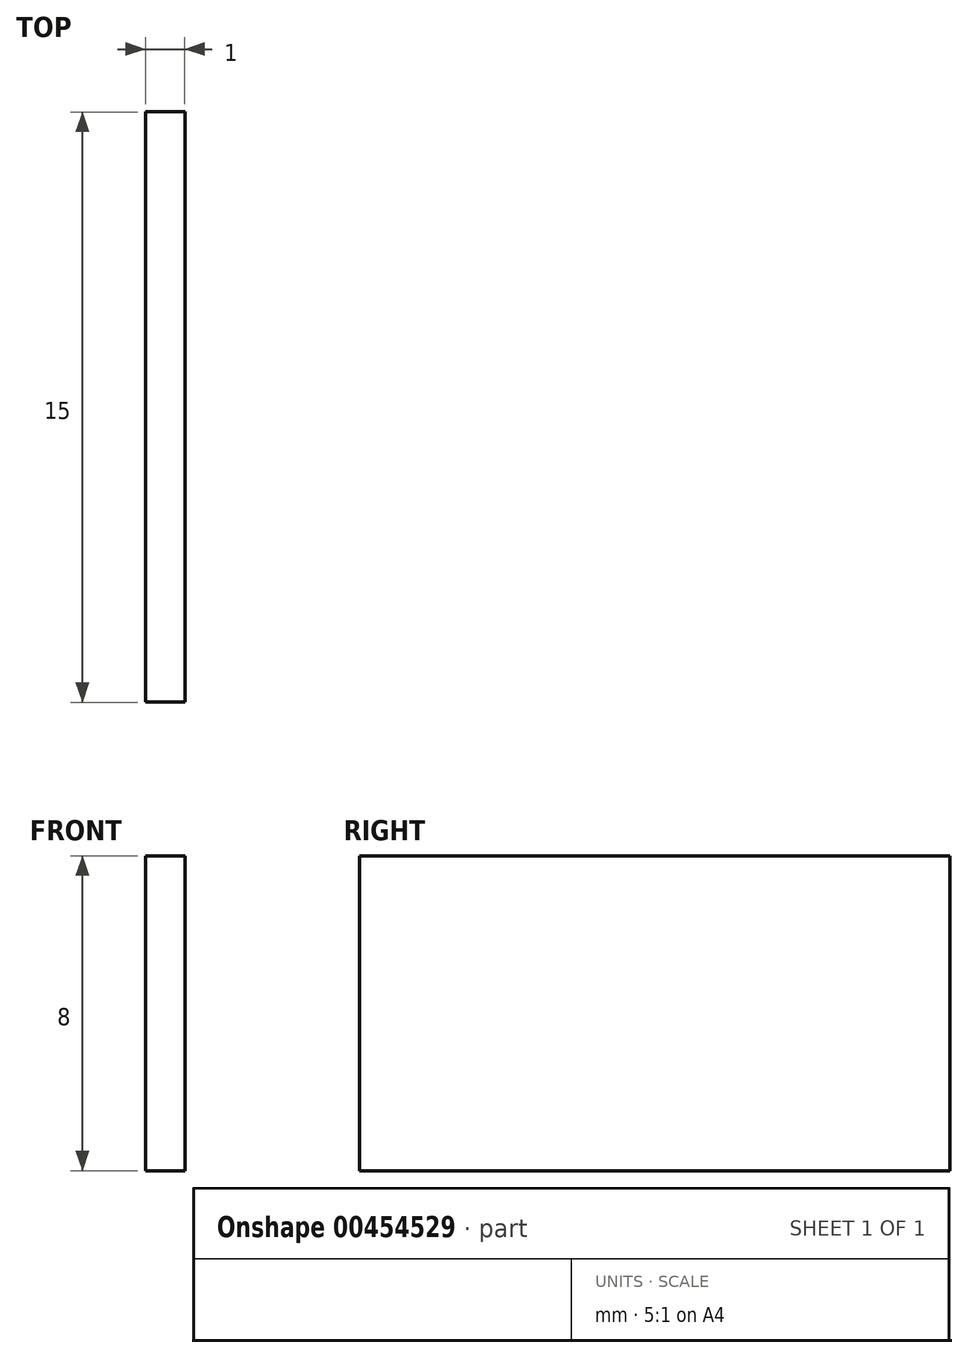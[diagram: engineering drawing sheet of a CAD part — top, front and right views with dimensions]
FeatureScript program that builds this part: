
annotation { "Feature Type Name" : "Feature", "Feature Type Description" : "" }
export const myFeature = defineFeature(function(context is Context, id is Id, definition is map)
    precondition{}
    {
        {
            var Q0;
            Q0=qCreatedBy(makeId("Top.planeOp"),FACE);
            var sketch = newSketch(context, id + "F0", { "sketchPlane" : qUnion([Q0])});
            skLineSegment(sketch, "E0.bottom", {"start": v(-9.98, -4.15) * mm, "end": v(-8.98, -4.15) * mm});
            skLineSegment(sketch, "E0.top", {"start": v(-9.98, -19.15) * mm, "end": v(-8.98, -19.15) * mm});
            skLineSegment(sketch, "E0.left", {"start": v(-9.98, -4.15) * mm, "end": v(-9.98, -19.15) * mm});
            skLineSegment(sketch, "E0.right", {"start": v(-8.98, -4.15) * mm, "end": v(-8.98, -19.15) * mm});
            skSolve(sketch);
        }
        {
            var Q0;
            Q0 = qSketchRegion(id + "F0", true);
            extrude(context, id + "F1", {"entities" : qUnion([Q0]), "depth" : 8 * mm});
        }
    });
